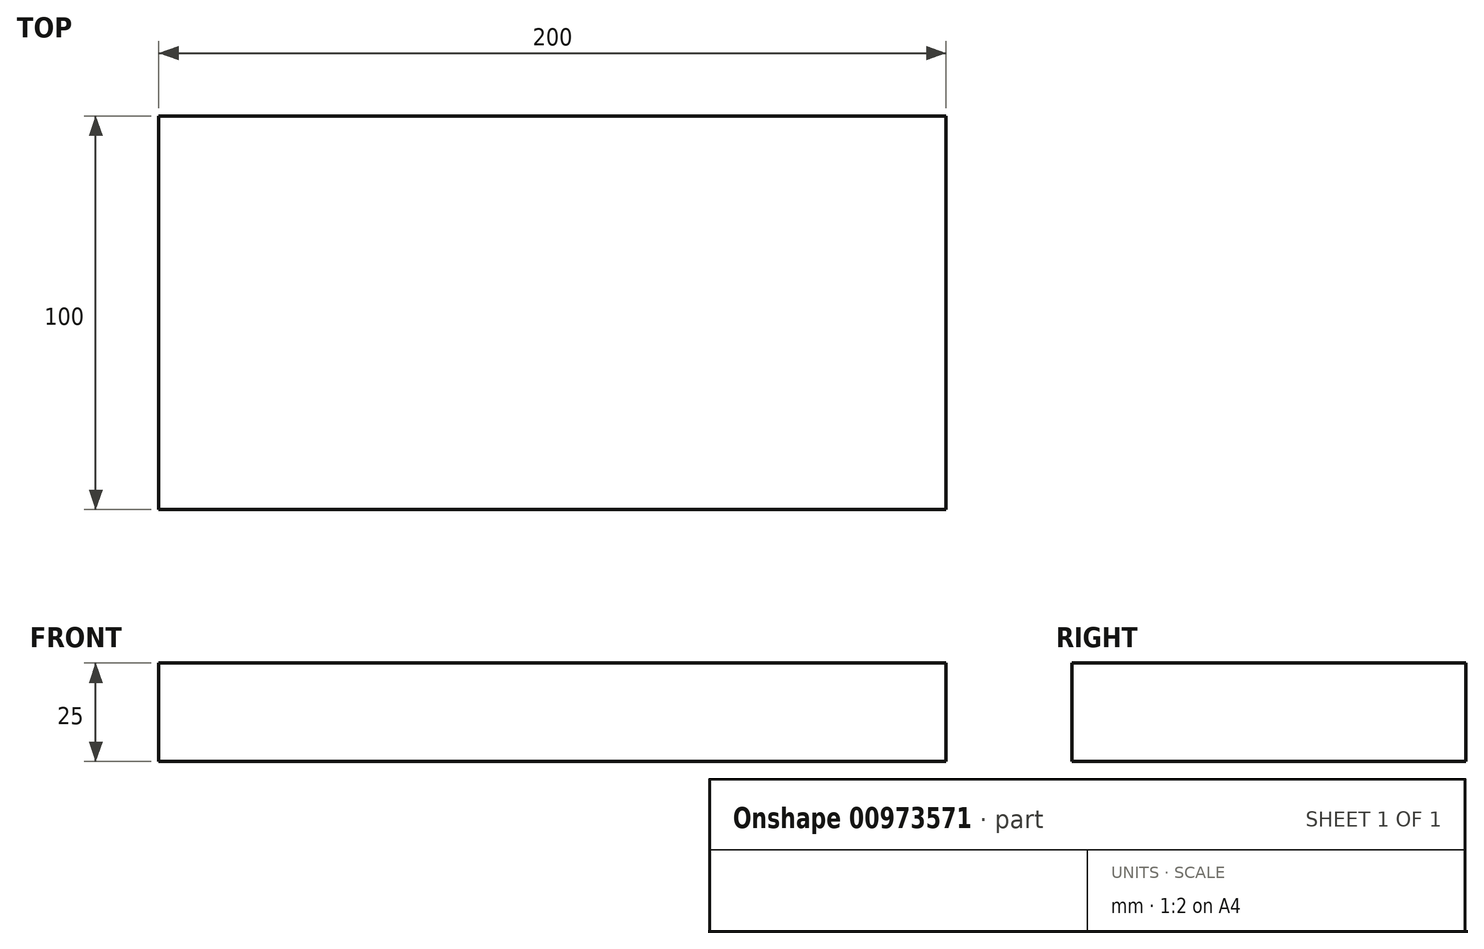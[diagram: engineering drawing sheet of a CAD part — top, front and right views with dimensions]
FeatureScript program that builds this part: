
annotation { "Feature Type Name" : "Feature", "Feature Type Description" : "" }
export const myFeature = defineFeature(function(context is Context, id is Id, definition is map)
    precondition{}
    {
        {
            var Q0;
            Q0=qCreatedBy(makeId("Top.planeOp"),FACE);
            var sketch = newSketch(context, id + "F0", { "sketchPlane" : qUnion([Q0])});
            skLineSegment(sketch, "E0.bottom", {"start": v(-31.88, 75.61) * mm, "end": v(168.12, 75.61) * mm});
            skLineSegment(sketch, "E0.top", {"start": v(-31.88, -24.39) * mm, "end": v(168.12, -24.39) * mm});
            skLineSegment(sketch, "E0.left", {"start": v(-31.88, 75.61) * mm, "end": v(-31.88, -24.39) * mm});
            skLineSegment(sketch, "E0.right", {"start": v(168.12, 75.61) * mm, "end": v(168.12, -24.39) * mm});
            skSolve(sketch);
        }
        {
            var Q0;
            Q0 = qSketchRegion(id + "F0", true);
            extrude(context, id + "F1", {"entities" : qUnion([Q0]), "depth" : 25 * mm, "offsetDistance" : 25 * mm});
        }
        {
            var Q0;
            Q0 = qSketchRegion(id + "F0", true);
            extrude(context, id + "F2", {"entities" : qUnion([Q0]), "operationType" : NewBodyOperationType.ADD, "depth" : 25 * mm, "offsetDistance" : 25 * mm});
        }
        {
            var Q0;
            Q0=makeQuery(id+"F0.imprint","IMPRINT",FACE,{"disambiguationData":[TD([[makeQuery(id+"F0.imprint","IMPRINT",EDGE,{"derivedFrom":sQuery(id+"F0.wireOp",EDGE,"E0.bottom")}),-1.0]])]});
            extrude(context, id + "F3", {"entities" : qUnion([Q0]), "operationType" : NewBodyOperationType.ADD, "depth" : 25 * mm, "offsetDistance" : 25 * mm});
        }
    });
